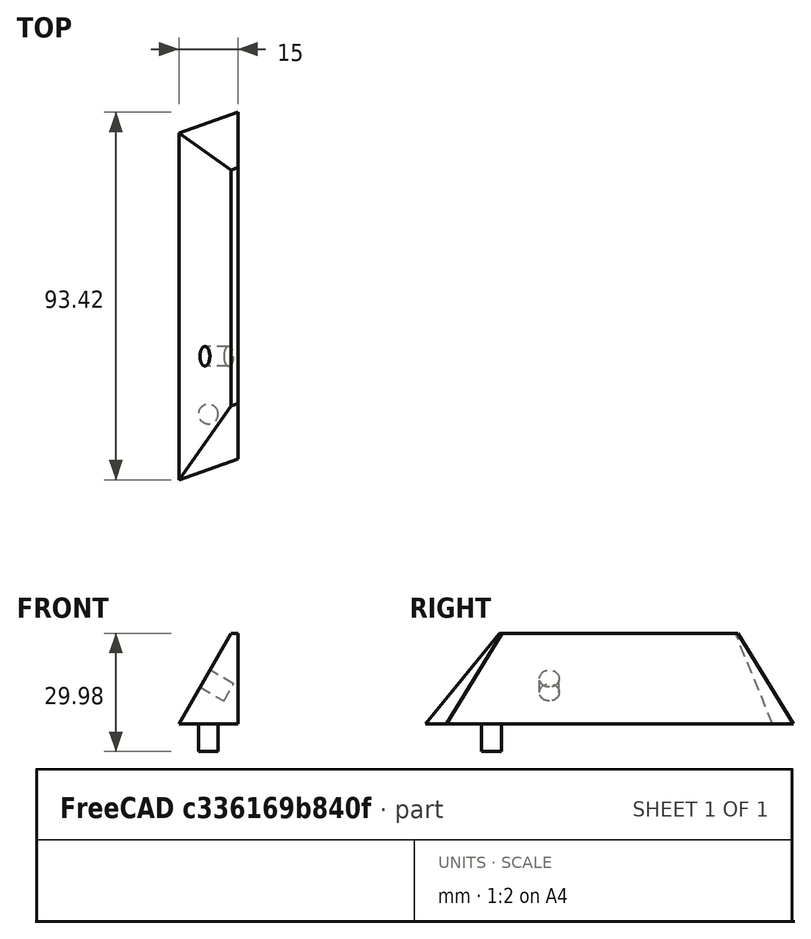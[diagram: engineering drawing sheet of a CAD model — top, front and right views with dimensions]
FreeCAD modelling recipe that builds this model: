
FCSTD DOCUMENT  (FreeCAD 1.0R39319 (Git))
Label: scorpius_part
License: All rights reserved
LicenseURL: https://en.wikipedia.org/wiki/All_rights_reserved
objects: TechDraw::DrawViewDimension×4, Sketcher::SketchObject×3, PartDesign::Plane×3, PartDesign::Pocket×3, TechDraw::DrawProjGroupItem×3, PartDesign::Pad×2, PartDesign::SubShapeBinder×1, PartDesign::Body×1, TechDraw::DrawSVGTemplate×1, TechDraw::DrawProjGroup×1, TechDraw::DrawPage×1
note: 31 computed .brp shape members not serialized (recipe doc carries the construction recipe); baked Part::Feature solids carry a one-line shape summary decoded from their .brp
EXTERNAL_REF file=rhombic-dodecahedron.FCStd obj=Body

FEATURE [Sketcher::SketchObject] Sketch  label="Profil"
  ArcFitTolerance = 1e-06
  AttachmentSupport = -> [XZ_Plane]
  FullyConstrained = true
  MakeInternals = false
  MapMode = 5
  Placement = pos=(0,0,0) rot=(1,0,0;1.5708rad)
  expr: .Constraints.Base = href(<<Body>>.Base) * 0.5
  expr: .Constraints.Side = 2 * .Constraints.Base
  sketch-geometry (5):
    g0: LineSegment StartX=0 StartY=0 StartZ=0 EndX=0 EndY=22.9808 EndZ=0
    g1: LineSegment StartX=0 StartY=22.9808 StartZ=0 EndX=-1.73205 EndY=22.9808 EndZ=0
    g2: LineSegment StartX=-1.73205 StartY=22.9808 StartZ=0 EndX=-15 EndY=0 EndZ=0
    g3: LineSegment StartX=-15 StartY=0 StartZ=0 EndX=0 EndY=0 EndZ=0
    g4: LineSegment [constr] StartX=-15 StartY=0 StartZ=0 EndX=0 EndY=25.9808 EndZ=0
  constraints (16):
    c: Coincident(g-1,g0)
    c: PointOnObject(g0,g-2)
    c: Coincident(g0,g1)
    c: Coincident(g1,g2)
    c: PointOnObject(g2,g-1)
    c: Coincident(g2,g3)
    c: Coincident(g3,g0)
    c: Distance(g3) = 15  'Base'
    c: Coincident(g4,g2)
    c: PointOnObject(g4,g-2)
    c: Distance(g4) = 30  'Side'
    c: DistanceY(g0,g4) = 3  'Cut'
    c: Horizontal(g1)
    c: PointOnObject(g1,g4)
    c: Distance(g1,g2) = 26.5359  'SideCut'
    c: DistanceY(g0,g0) = 22.9808  'Hauteur'
FEATURE [PartDesign::Pad] Pad  label="Corp"
  Direction = (0,-1,2e-16)
  Length = 120
  Length2 = 10
  Midplane = true
  Placement = pos=(0,0,0) rot=(1,0,0;1.5708rad)
  Profile = -> Sketch
  ReferenceAxis = -> Sketch [N_Axis]
  Refine = true
  Suppressed = false
  Type = 0
FEATURE [PartDesign::Plane] DatumPlane
  AttachmentSupport = -> [Pad]
  Length = 63.6688
  MapMode = 5
  Placement = pos=(0,0,-2e-16) rot=(1,0,0;3.14159rad)
  ResizeMode = 0
  Width = 107.087
FEATURE [Sketcher::SketchObject] Sketch001  label="BasePiece"
  ArcFitTolerance = 1e-06
  AttachmentSupport = -> [DatumPlane]
  ExternalGeometry = -> [Pad]
  FullyConstrained = true
  MakeInternals = false
  MapMode = 5
  Placement = pos=(0,0,-2e-16) rot=(1,0,0;3.14159rad)
  expr: Constraints[14] = href(<<Body>>.Base)
  expr: Constraints[19] = acos(1 / 3)
  expr: Constraints[25] = <<Profil>>.Constraints.SideCut
  sketch-geometry (16):
    g0: LineSegment [constr] StartX=-15 StartY=21.2132 StartZ=0 EndX=15 EndY=10.6066 EndZ=0
    g1: LineSegment [constr] StartX=15 StartY=10.6066 StartZ=0 EndX=15 EndY=-21.2132 EndZ=0
    g2: LineSegment [constr] StartX=15 StartY=-21.2132 StartZ=0 EndX=-15 EndY=-10.6066 EndZ=0
    g3: LineSegment [constr] StartX=-15 StartY=-10.6066 StartZ=0 EndX=-15 EndY=21.2132 EndZ=0
    g4: LineSegment [constr] StartX=-15 StartY=-10.6066 StartZ=0 EndX=15 EndY=10.6066 EndZ=0
    g5: LineSegment [constr] StartX=-15 StartY=-10.6066 StartZ=0 EndX=15 EndY=-10.6066 EndZ=0
    g6: GeomPoint [constr] X=15 Y=-10.6066 Z=0
    g7: GeomPoint [constr] X=0 Y=15.9099 Z=0
    g8: LineSegment [constr] StartX=-15 StartY=49.3588 StartZ=0 EndX=0 EndY=44.0555 EndZ=0
    g9: LineSegment [constr] StartX=-15 StartY=49.3588 StartZ=0 EndX=-23.8453 EndY=24.3405 EndZ=0
    g10: LineSegment [constr] StartX=-15 StartY=49.3588 StartZ=0 EndX=0 EndY=15.9099 EndZ=0
    g11: LineSegment [constr] StartX=0 StartY=44.0555 StartZ=0 EndX=-15 EndY=21.2132 EndZ=0
    g12: GeomPoint [constr] X=-7.5 Y=32.6343 Z=0
    g13: Circle CenterX=-7.5 CenterY=32.6343 CenterZ=0 NormalX=0 NormalY=0 NormalZ=1 AngleXU=0 Radius=2.5
    g14: LineSegment [constr] StartX=0 StartY=15.9099 StartZ=0 EndX=-15 EndY=15.9099 EndZ=0
    g15: LineSegment [constr] StartX=-15 StartY=21.2132 StartZ=0 EndX=15 EndY=-21.2132 EndZ=0
  constraints (43):
    c: PointOnObject(g0,g-3)
    c: Vertical(g1)
    c: Coincident(g2,g1)
    c: PointOnObject(g2,g-3)
    c: Coincident(g3,g2)
    c: Coincident(g3,g0)
    c: Equal(g0,g1)
    c: Parallel(g0,g2)
    c: Coincident(g4,g2)
    c: Coincident(g4,g0)
    c: PointOnObject(g-1,g4)
    c: Coincident(g1,g0)
    c: Coincident(g5,g2)
    c: Horizontal(g5)
    c: Distance(g5) = 30
    c: Distance(g-4) = 120
    c: PointOnObject(g6,g1)
    c: Coincident(g5,g6)
    c: Symmetric(g0,g0,g7)
    c: Angle(g1,g2) = 1.23096
    c: PointOnObject(g8,g-3)
    c: PointOnObject(g8,g-4)
    c: Parallel(g0,g8)
    c: PointOnObject(g9,g0)
    c: Perpendicular(g9,g8)
    c: Distance(g9) = 26.5359
    c: Coincident(g8,g9)
    c: Coincident(g10,g8)
    c: Coincident(g10,g7)
    c: Coincident(g11,g8)
    c: PointOnObject(g12,g11)
    c: PointOnObject(g12,g10)
    c: Diameter(g13) = 5
    c: Coincident(g13,g12)
    c: Coincident(g11,g0)
    c: Distance(g3) = 31.8198  'Hauteur'
    c: Coincident(g14,g7)
    c: PointOnObject(g14,g3)
    c: Horizontal(g14)
    c: Distance(g0,g14) = 5.3033  'PositionRefTrou'
    c: Coincident(g15,g0)
    c: Coincident(g15,g1)
    c: Distance(g15) = 51.9615  'RhombusLong'
FEATURE [PartDesign::Pad] Pad001
  BaseFeature = -> Pad
  Direction = (0,0,-1)
  Length = 7
  Length2 = 10
  Placement = pos=(0,0,0) rot=(1,0,0;1.5708rad)
  Profile = -> Sketch001
  ReferenceAxis = -> Sketch001 [N_Axis]
  Refine = true
  Suppressed = false
  Type = 0
FEATURE [Sketcher::SketchObject] Sketch002
  ArcFitTolerance = 1e-06
  AttachmentSupport = -> [Pad001]
  ExternalGeometry = -> [Pad001]
  FullyConstrained = true
  MakeInternals = false
  MapMode = 5
  Placement = pos=(-11.25,2.9e-15,6.49519) rot=(-0.5,0,0.866025;3.14159rad)
  expr: Constraints[12] = href(<<Body>>.Base) * 0.5
  expr: Constraints[21] = <<BasePiece>>.Constraints.PositionRefTrou
  expr: Constraints[28] = acos(1 / 3)
  sketch-geometry (13):
    g0: GeomPoint [constr] X=7.5 Y=5.3033 Z=0
    g1: LineSegment [constr] StartX=7.5 StartY=5.3033 StartZ=0 EndX=-19.0359 EndY=14.6852 EndZ=0
    g2: LineSegment [constr] StartX=-19.0359 StartY=14.6852 StartZ=0 EndX=-19.0359 EndY=30.5951 EndZ=0
    g3: LineSegment [constr] StartX=-19.0359 StartY=30.5951 StartZ=0 EndX=7.5 EndY=21.2132 EndZ=0
    g4: LineSegment [constr] StartX=7.5 StartY=21.2132 StartZ=0 EndX=7.5 EndY=5.3033 EndZ=0
    g5: LineSegment [constr] StartX=7.5 StartY=21.2132 StartZ=0 EndX=2.5 EndY=7.07107 EndZ=0
    g6: LineSegment [constr] StartX=7.5 StartY=21.2132 StartZ=0 EndX=-19.0359 EndY=14.6852 EndZ=0
    g7: GeomPoint [constr] X=-5.76795 Y=17.9492 Z=0
    g8: Circle CenterX=-5.76795 CenterY=17.9492 CenterZ=0 NormalX=0 NormalY=0 NormalZ=1 AngleXU=0 Radius=2.5
    g9: GeomPoint X=7.5 Y=5.3033 Z=0
    g10: GeomPoint X=7.5 Y=-1.9e-15 Z=0
    g11: LineSegment [constr] StartX=-19.0359 StartY=30.5951 StartZ=0 EndX=7.5 EndY=5.3033 EndZ=0
    g12: LineSegment [constr] StartX=7.5 StartY=21.2132 StartZ=0 EndX=7.5 EndY=5.3033 EndZ=0
  constraints (29):
    c: Coincident(g1,g0)
    c: PointOnObject(g1,g-4)
    c: Coincident(g1,g2)
    c: PointOnObject(g2,g-4)
    c: Coincident(g2,g3)
    c: PointOnObject(g3,g-3)
    c: Coincident(g3,g4)
    c: Coincident(g4,g0)
    c: Parallel(g3,g1)
    c: Coincident(g5,g3)
    c: PointOnObject(g5,g1)
    c: Perpendicular(g1,g5)
    c: Distance(g5) = 15
    c: Coincident(g6,g3)
    c: Coincident(g6,g1)
    c: PointOnObject(g7,g6)
    c: Diameter(g8) = 5
    c: Coincident(g8,g7)
    c: PointOnObject(g9,g-3)
    c: Symmetric(g-3,g-3,g10)
    c: DistanceY(g-3,g-3) = 120
    c: DistanceY(g10,g9) = 5.3033
    c: Coincident(g0,g9)
    c: Coincident(g11,g2)
    c: Coincident(g11,g0)
    c: PointOnObject(g7,g11)
    c: Coincident(g12,g3)
    c: Coincident(g12,g0)
    c: Angle(g2,g3) = 1.23096
FEATURE [PartDesign::Pocket] Pocket
  BaseFeature = -> Pad001
  Direction = (0.866025,0,-0.5)
  Length = 7
  Length2 = 5
  Placement = pos=(0,0,0) rot=(1,0,0;1.5708rad)
  Profile = -> Sketch002
  ReferenceAxis = -> Sketch002 [N_Axis]
  Refine = true
  Suppressed = false
  Type = 0
FEATURE [PartDesign::SubShapeBinder] Binder
  BindCopyOnChange = 0
  BindMode = 0
  ClaimChildren = false
  Context = -> Body [Binder.]
  Fuse = false
  MakeFace = true
  OffsetFill = false
  OffsetIntersection = false
  OffsetJoinType = 0
  OffsetOpenResult = false
  PartialLoad = false
  Placement = pos=(0,0,-25.9808) rot=(0.769315,-0.244485,-0.590238;0.987816rad)
  Refine = true
  Relative = true
  Support = -> [<external rhombic-dodecahedron.FCStd>#Body]
  _Version = 2
  expr: .Placement.Base.z = -<<BasePiece>>.Constraints.RhombusLong / 2
FEATURE [PartDesign::Plane] DatumPlane001  label="TronqueTete"
  AttachmentOffset = pos=(0,0,72.9808) rot=(0,0,1;0rad)
  AttachmentSupport = -> [Binder]
  Length = 85.6205
  MapMode = 5
  Placement = pos=(28.5739,-80.7996,23.5) rot=(0.863946,0.447253,-0.231434;1.07957rad)
  ResizeMode = 0
  Width = 127.016
  expr: .AttachmentOffset.Base.z = <<Profil>>.Constraints.Hauteur + 50 mm
FEATURE [PartDesign::Pocket] Pocket001
  BaseFeature = -> Pocket
  Direction = (-0.288738,0.816474,-0.5)
  Length = 50
  Length2 = 5
  Placement = pos=(0,0,0) rot=(1,0,0;1.5708rad)
  Profile = -> DatumPlane001
  Refine = true
  Suppressed = false
  Type = 0
FEATURE [PartDesign::Plane] DatumPlane002  label="TronqueQueue"
  AttachmentOffset = pos=(0,0,72.9808) rot=(0,0,1;0rad)
  AttachmentSupport = -> [Binder]
  Length = 85.6205
  MapMode = 5
  Placement = pos=(-28.5739,80.7996,23.5) rot=(-0.231511,0.447203,0.863951;2.90313rad)
  ResizeMode = 0
  Width = 127.016
  expr: .AttachmentOffset.Base.z = <<Profil>>.Constraints.Hauteur + 50 mm
FEATURE [PartDesign::Pocket] Pocket002
  BaseFeature = -> Pocket001
  Direction = (0.288738,-0.816474,-0.5)
  Length = 50
  Length2 = 5
  Placement = pos=(0,0,0) rot=(1,0,0;1.5708rad)
  Profile = -> DatumPlane002
  Refine = true
  Suppressed = false
  Type = 0
FEATURE [PartDesign::Body] Body
  AllowCompound = false
  Base = 30
  Group = -> [Sketch,Pad,DatumPlane,Sketch001,Pad001,Sketch002,Pocket,Binder,DatumPlane001,Pocket001,DatumPlane002,Pocket002]
  Origin = -> Origin
  Tip = -> Pocket002
FEATURE [TechDraw::DrawSVGTemplate] Template
  EditableTexts = approval_person=B. Hecate; creator=A. Nemesis; date_of_issue=11/10/2025; document_type=Component Drawing; general_tolerances=ISO 2768-m; identification_number=DN; language_code=EN; part_material=Stainless steel Mat.No. 1.4301; revision_index=AAA; scale=1 : 1; sheet_number=1 / 1; title=scorpius_part
  Height = 297
  Orientation = 0
  Template = <userpath>/AppData/Local/Programs/FreeCAD 1.0/data/Mod/TechDraw/Templates/A4_Portrait_ISO5457_minimal.svg
  Width = 210
FEATURE [TechDraw::DrawProjGroupItem] View  label="Front"
  CoarseView = false
  Direction = (0,-1,0)
  Focus = 100
  HardHidden = true
  IsoCount = 0
  IsoHidden = false
  IsoVisible = false
  LockPosition = true
  Perspective = false
  Rotation = 0
  RotationVector = (1,0,0)
  ScaleType = 2
  ScrubCount = 1
  SeamHidden = false
  SeamVisible = false
  SmoothHidden = false
  SmoothVisible = true
  Source = -> [Body]
  Type = 0
  X = 0
  XDirection = (1,0,0)
  Y = 0
FEATURE [TechDraw::DrawProjGroupItem] ProjItem  label="Left"
  CoarseView = false
  Direction = (-1,-1e-16,0)
  Focus = 100
  HardHidden = true
  IsoCount = 0
  IsoHidden = false
  IsoVisible = false
  LockPosition = false
  Perspective = false
  Rotation = 0
  RotationVector = (1,0,0)
  ScaleType = 0
  ScrubCount = 1
  SeamHidden = false
  SeamVisible = false
  SmoothHidden = false
  SmoothVisible = true
  Source = -> [Body]
  Type = 1
  X = 69.209
  XDirection = (1e-16,-1,0)
  Y = 0
FEATURE [TechDraw::DrawProjGroupItem] ProjItem001  label="Bottom"
  CoarseView = false
  Direction = (0,0,-1)
  Focus = 100
  HardHidden = true
  IsoCount = 0
  IsoHidden = false
  IsoVisible = false
  LockPosition = false
  Perspective = false
  Rotation = 0
  RotationVector = (1,0,0)
  ScaleType = 0
  ScrubCount = 1
  SeamHidden = false
  SeamVisible = false
  SmoothHidden = false
  SmoothVisible = true
  Source = -> [Body]
  Type = 5
  X = 0
  XDirection = (1,0,0)
  Y = 76.6993
FEATURE [TechDraw::DrawProjGroup] ProjGroup
  Anchor = -> View
  AutoDistribute = true
  LockPosition = false
  ProjectionType = 0
  Rotation = 0
  ScaleType = 0
  Source = -> [Body]
  Views = -> [View,ProjItem,ProjItem001]
  X = 56.9286
  Y = 125.715
  spacingX = 15
  spacingY = 15
FEATURE [TechDraw::DrawViewDimension] Dimension
  AngleOverride = false
  Arbitrary = false
  ArbitraryTolerances = false
  BoxCorners = (2) [(-7.5,-14.9904,-1e-07),(7.5,14.9904,1e-07)]
  EqualTolerance = true
  ExtensionAngle = 0
  FormatSpec = %.2w
  FormatSpecOverTolerance = %+.2w
  FormatSpecUnderTolerance = %+.2w
  Inverted = false
  LineAngle = 0
  LockPosition = false
  MeasureType = 1
  OverTolerance = 0
  References2D = -> [View]
  Rotation = 0
  ScaleType = 0
  TheoreticalExact = false
  Type = 1
  UnderTolerance = 0
  X = 3.43993
  Y = -41.7419
FEATURE [TechDraw::DrawViewDimension] Dimension001
  AngleOverride = false
  Arbitrary = false
  ArbitraryTolerances = false
  BoxCorners = (2) [(-7.5,-14.9904,-1e-07),(7.5,14.9904,1e-07)]
  EqualTolerance = true
  ExtensionAngle = 0
  FormatSpec = %.2w
  FormatSpecOverTolerance = %+.2w
  FormatSpecUnderTolerance = %+.2w
  Inverted = false
  LineAngle = 0
  LockPosition = false
  MeasureType = 1
  OverTolerance = 0
  References2D = -> [View]
  Rotation = 0
  ScaleType = 0
  TheoreticalExact = false
  Type = 0
  UnderTolerance = 0
  X = -25.6001
  Y = 17.7802
FEATURE [TechDraw::DrawViewDimension] Dimension002
  AngleOverride = false
  Arbitrary = false
  ArbitraryTolerances = false
  BoxCorners = (2) [(-7.5,-46.709,0),(7.5,46.709,0)]
  EqualTolerance = true
  ExtensionAngle = 0
  FormatSpec = %.2w
  FormatSpecOverTolerance = %+.2w
  FormatSpecUnderTolerance = %+.2w
  Inverted = false
  LineAngle = 0
  LockPosition = false
  MeasureType = 1
  OverTolerance = 0
  References2D = -> [ProjItem001]
  Rotation = 0
  ScaleType = 0
  TheoreticalExact = false
  Type = 0
  UnderTolerance = 0
  X = -25.445
  Y = 2.6523
FEATURE [TechDraw::DrawViewDimension] Dimension003
  AngleOverride = false
  Arbitrary = false
  ArbitraryTolerances = false
  BoxCorners = (2) [(-46.709,-14.9904,-1e-07),(46.709,14.9904,1e-07)]
  EqualTolerance = true
  ExtensionAngle = 0
  FormatSpec = %.2w
  FormatSpecOverTolerance = %+.2w
  FormatSpecUnderTolerance = %+.2w
  Inverted = false
  LineAngle = 0
  LockPosition = false
  MeasureType = 1
  OverTolerance = 0
  References2D = -> [ProjItem]
  Rotation = 0
  ScaleType = 0
  TheoreticalExact = false
  Type = 1
  UnderTolerance = 0
  X = 22.6395
  Y = -38.4426
FEATURE [TechDraw::DrawPage] Page
  KeepUpdated = true
  NextBalloonIndex = 1
  ProjectionType = 0
  Template = -> Template
  Views = -> [ProjGroup,Dimension,Dimension001,Dimension002,Dimension003]
